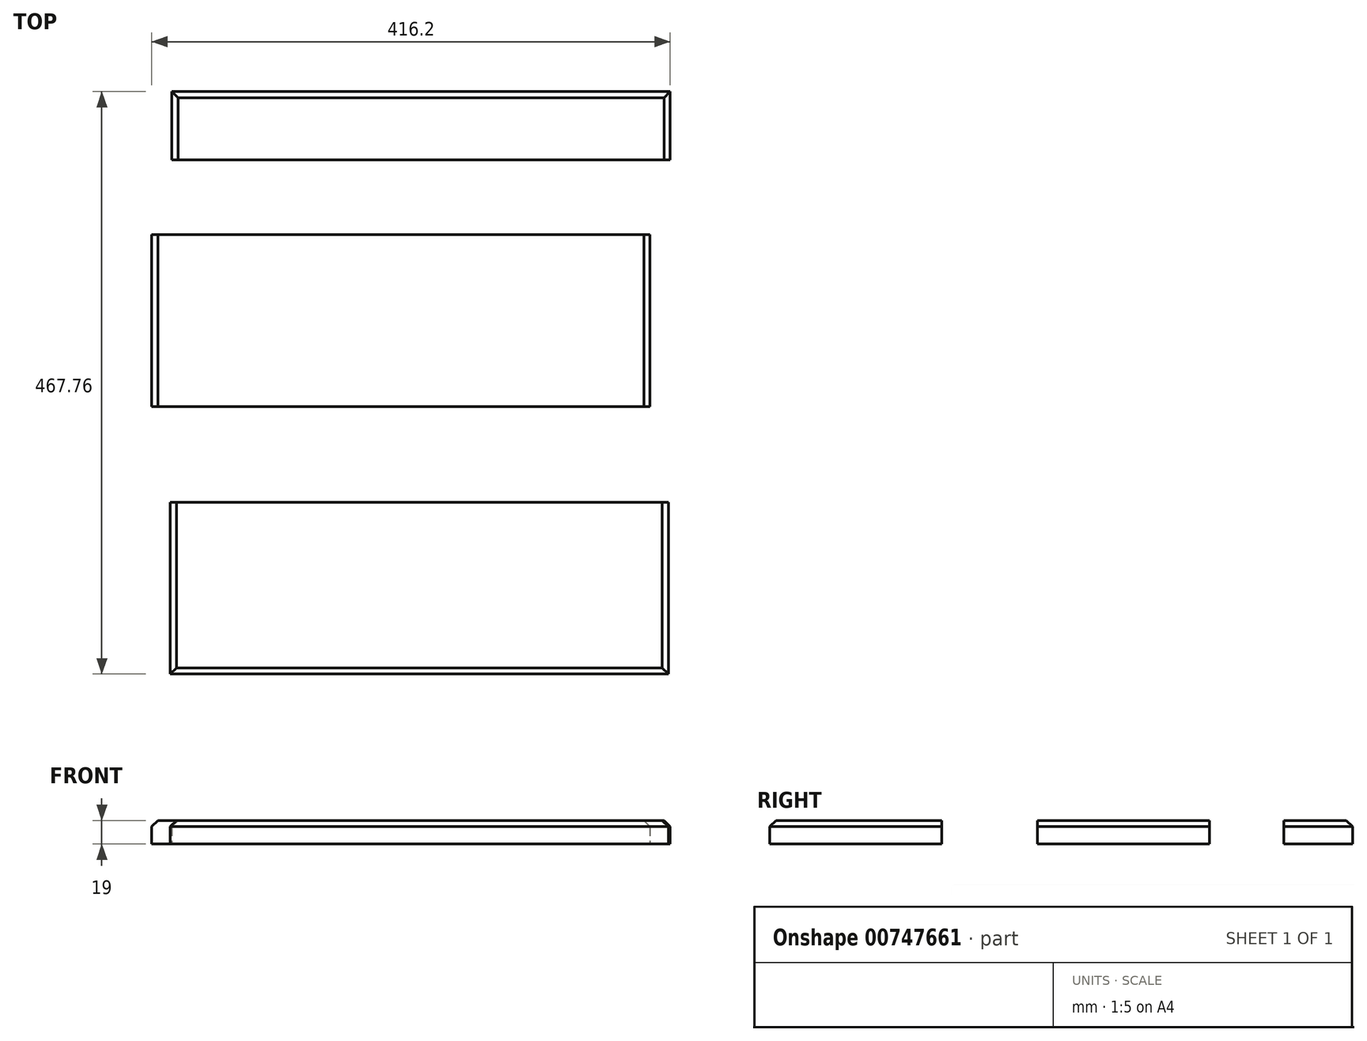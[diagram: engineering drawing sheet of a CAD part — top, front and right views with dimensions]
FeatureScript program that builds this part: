
annotation { "Feature Type Name" : "Feature", "Feature Type Description" : "" }
export const myFeature = defineFeature(function(context is Context, id is Id, definition is map)
    precondition{}
    {
        {
            var Q0;
            Q0=qCreatedBy(makeId("Top.planeOp"),FACE);
            var sketch = newSketch(context, id + "F0", { "sketchPlane" : qUnion([Q0])});
            skLineSegment(sketch, "E0.bottom", {"start": v(-271.78, 126.3) * mm, "end": v(128.22, 126.3) * mm});
            skLineSegment(sketch, "E0.top", {"start": v(-271.78, 71.3) * mm, "end": v(128.22, 71.3) * mm});
            skLineSegment(sketch, "E0.left", {"start": v(-271.78, 126.3) * mm, "end": v(-271.78, 71.3) * mm});
            skLineSegment(sketch, "E0.right", {"start": v(128.22, 126.3) * mm, "end": v(128.22, 71.3) * mm});
            skLineSegment(sketch, "E1.bottom", {"start": v(-287.98, -126.62) * mm, "end": v(112.02, -126.62) * mm});
            skLineSegment(sketch, "E1.top", {"start": v(-287.98, 11.38) * mm, "end": v(112.02, 11.38) * mm});
            skLineSegment(sketch, "E1.left", {"start": v(-287.98, -126.62) * mm, "end": v(-287.98, 11.38) * mm});
            skLineSegment(sketch, "E1.right", {"start": v(112.02, -126.62) * mm, "end": v(112.02, 11.38) * mm});
            skLineSegment(sketch, "E2.bottom", {"start": v(-273.07, -341.45) * mm, "end": v(126.93, -341.45) * mm});
            skLineSegment(sketch, "E2.top", {"start": v(-273.07, -203.45) * mm, "end": v(126.93, -203.45) * mm});
            skLineSegment(sketch, "E2.left", {"start": v(-273.07, -341.45) * mm, "end": v(-273.07, -203.45) * mm});
            skLineSegment(sketch, "E2.right", {"start": v(126.93, -341.45) * mm, "end": v(126.93, -203.45) * mm});
            skSolve(sketch);
        }
        {
            var Q0;
            Q0 = qSketchRegion(id + "F0", true);
            extrude(context, id + "F1", {"entities" : qUnion([Q0]), "depth" : 19 * mm, "offsetDistance" : 25 * mm});
        }
        {
            var Q0;
            Q0=makeQuery(id+"F1.opExtrude","CAP_EDGE",EDGE,{"disambiguationData":[OSD([sQuery(id+"F0.wireOp",EDGE,"E2.left")])],"isStart":false});
            var Q1;
            Q1=makeQuery(id+"F1.opExtrude","CAP_EDGE",EDGE,{"disambiguationData":[OSD([sQuery(id+"F0.wireOp",EDGE,"E2.bottom")])],"isStart":false});
            var Q2;
            Q2=makeQuery(id+"F1.opExtrude","CAP_EDGE",EDGE,{"disambiguationData":[OSD([sQuery(id+"F0.wireOp",EDGE,"E2.right")])],"isStart":false});
            var Q3;
            Q3=makeQuery(id+"F1.opExtrude","CAP_EDGE",EDGE,{"disambiguationData":[OSD([sQuery(id+"F0.wireOp",EDGE,"E1.right")])],"isStart":false});
            var Q4;
            Q4=makeQuery(id+"F1.opExtrude","CAP_EDGE",EDGE,{"disambiguationData":[OSD([sQuery(id+"F0.wireOp",EDGE,"E1.left")])],"isStart":false});
            var Q5;
            Q5=makeQuery(id+"F1.opExtrude","CAP_EDGE",EDGE,{"disambiguationData":[OSD([sQuery(id+"F0.wireOp",EDGE,"E0.left")])],"isStart":false});
            var Q6;
            Q6=makeQuery(id+"F1.opExtrude","CAP_EDGE",EDGE,{"disambiguationData":[OSD([sQuery(id+"F0.wireOp",EDGE,"E0.bottom")])],"isStart":false});
            var Q7;
            Q7=makeQuery(id+"F1.opExtrude","CAP_EDGE",EDGE,{"disambiguationData":[OSD([sQuery(id+"F0.wireOp",EDGE,"E0.right")])],"isStart":false});
            chamfer(context, id + "F2", {"entities" : qUnion([Q0, Q1, Q2, Q3, Q4, Q5, Q6, Q7]), "width" : 5 * mm, "tangentPropagation" : true});
        }
    });
